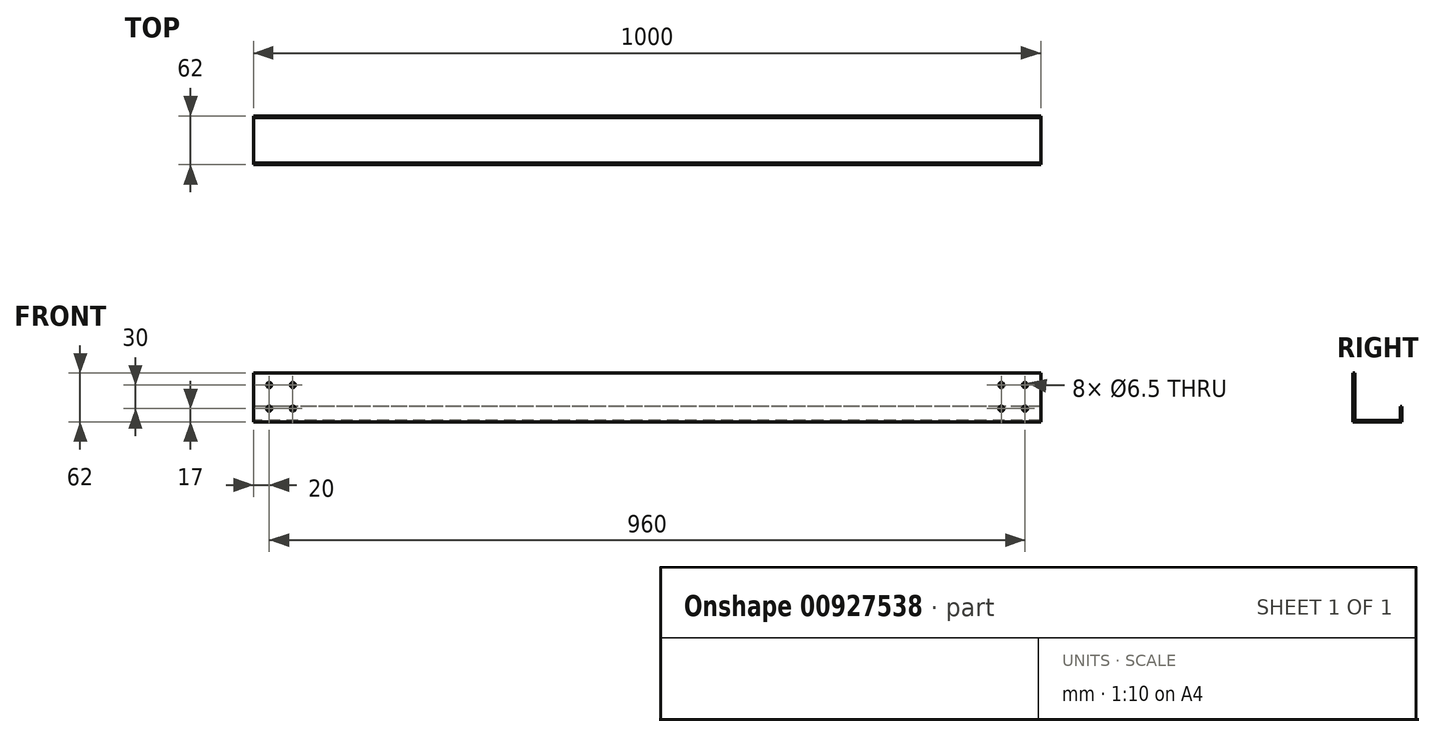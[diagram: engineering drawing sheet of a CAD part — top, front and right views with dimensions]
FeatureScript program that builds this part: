
annotation { "Feature Type Name" : "Feature", "Feature Type Description" : "" }
export const myFeature = defineFeature(function(context is Context, id is Id, definition is map)
    precondition{}
    {
        {
            var Q0;
            Q0=qCreatedBy(makeId("Right.planeOp"),FACE);
            var sketch = newSketch(context, id + "F0", { "sketchPlane" : qUnion([Q0])});
            skLineSegment(sketch, "E0", {"start": v(0, 0) * mm, "end": v(62, 0) * mm});
            skLineSegment(sketch, "E1", {"start": v(0, 0) * mm, "end": v(0, 62) * mm});
            skLineSegment(sketch, "E2.0", {"start": v(2, 2) * mm, "end": v(2, 62) * mm});
            skLineSegment(sketch, "E3.0", {"start": v(2, 2) * mm, "end": v(60, 2) * mm});
            skLineSegment(sketch, "E4", {"start": v(0, 62) * mm, "end": v(2, 62) * mm});
            skLineSegment(sketch, "E5", {"start": v(60, 2) * mm, "end": v(60, 20) * mm});
            skLineSegment(sketch, "E6.0", {"start": v(62, 0) * mm, "end": v(62, 20) * mm});
            skLineSegment(sketch, "E7", {"start": v(60, 20) * mm, "end": v(62, 20) * mm});
            skSolve(sketch);
        }
        {
            var Q0;
            Q0 = qSketchRegion(id + "F0", true);
            extrude(context, id + "F1", {"entities" : qUnion([Q0]), "depth" : 1000 * mm, "offsetDistance" : 25 * mm});
        }
        {
            var Q0;
            Q0=makeQuery(id+"F1.opExtrude","SWEPT_FACE",FACE,{"disambiguationData":[OSD([sQuery(id+"F0.wireOp",EDGE,"E2.0")])]});
            var sketch = newSketch(context, id + "F2", { "sketchPlane" : qUnion([Q0])});
            skLineSegment(sketch, "E8", {"start": v(-1015.7, 32) * mm, "end": v(47, 32) * mm, "construction": true});
            skPoint(sketch, "E8.startSnap0", {"position": v(-1000, 32) * mm});
            skCircle(sketch, "E9", {"center": v(-980, 47) * mm, "radius": 3.25 * mm});
            skCircle(sketch, "E10", {"center": v(-950, 47) * mm, "radius": 3.25 * mm});
            skCircle(sketch, "E11.MirrorC", {"center": v(-980, 17) * mm, "radius": 3.25 * mm});
            skCircle(sketch, "E12.MirrorC", {"center": v(-950, 17) * mm, "radius": 3.25 * mm});
            skLineSegment(sketch, "E13", {"start": v(-500, 214.34) * mm, "end": v(-500, -181.94) * mm, "construction": true});
            skPoint(sketch, "E13.startSnap0", {"position": v(-500, 62) * mm});
            skCircle(sketch, "E14.MirrorC", {"center": v(-50, 47) * mm, "radius": 3.25 * mm});
            skCircle(sketch, "E15.MirrorC", {"center": v(-20, 47) * mm, "radius": 3.25 * mm});
            skCircle(sketch, "E16.MirrorC", {"center": v(-20, 17) * mm, "radius": 3.25 * mm});
            skCircle(sketch, "E17.MirrorC", {"center": v(-50, 17) * mm, "radius": 3.25 * mm});
            skLineSegment(sketch, "E18", {"start": v(-250, 220.57) * mm, "end": v(-250, -221.82) * mm, "construction": true});
            skLineSegment(sketch, "E19", {"start": v(-750, 267.3) * mm, "end": v(-750, -213.72) * mm, "construction": true});
            skSolve(sketch);
        }
        {
            var Q0;
            Q0 = qSketchRegion(id + "F2", true);
            extrude(context, id + "F3", {"entities" : qUnion([Q0]), "operationType" : NewBodyOperationType.REMOVE, "oppositeDirection" : true, "depth" : 25 * mm, "offsetDistance" : 25 * mm});
        }
    });
